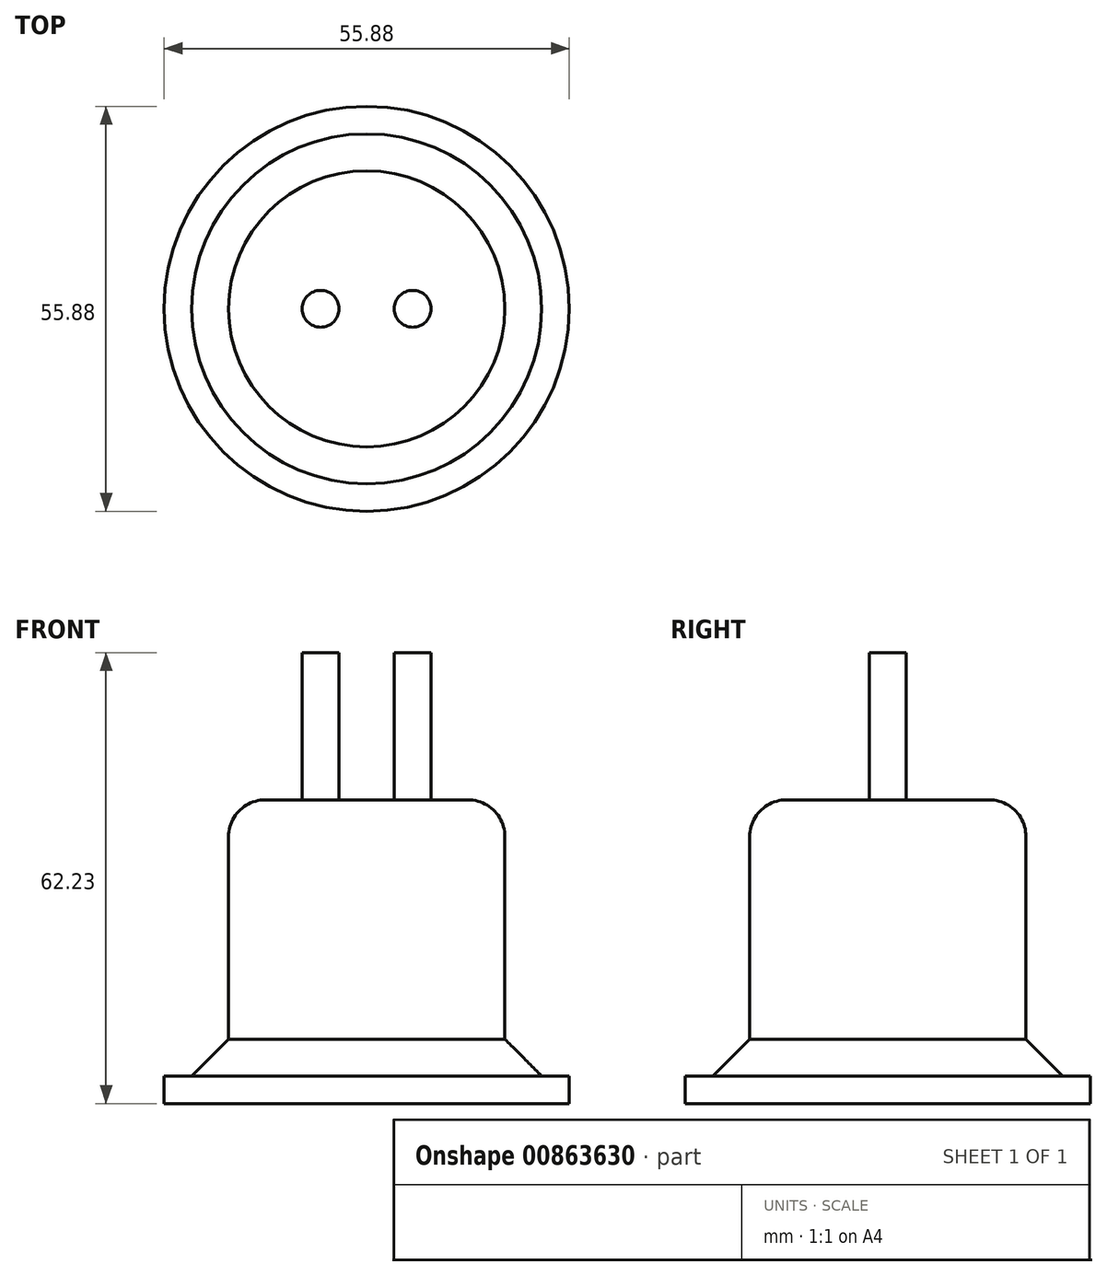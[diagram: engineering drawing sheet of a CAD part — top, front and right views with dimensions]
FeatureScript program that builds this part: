
annotation { "Feature Type Name" : "Feature", "Feature Type Description" : "" }
export const myFeature = defineFeature(function(context is Context, id is Id, definition is map)
    precondition{}
    {
        {
            var Q0;
            Q0=qCreatedBy(makeId("Top.planeOp"),FACE);
            var sketch = newSketch(context, id + "F0", { "sketchPlane" : qUnion([Q0])});
            skPoint(sketch, "E0.middle", {"position": v(0, 0) * mm});
            skCircle(sketch, "E1", {"center": v(0, 0) * mm, "radius": 27.94 * mm});
            skSolve(sketch);
        }
        {
            var Q0;
            Q0 = qSketchRegion(id + "F0", true);
            extrude(context, id + "F1", {"entities" : qUnion([Q0]), "depth" : 3.8 * mm, "offsetDistance" : 25.4 * mm});
        }
        {
            var Q0;
            Q0=makeQuery(id+"F1.opExtrude","CAP_FACE",FACE,{"disambiguationData":[OSD([sQuery(id+"F0.wireOp",EDGE,"E1")])],"isStart":false});
            var sketch = newSketch(context, id + "F2", { "sketchPlane" : qUnion([Q0])});
            skCircle(sketch, "E2", {"center": v(0, 0) * mm, "radius": 19.05 * mm});
            skSolve(sketch);
        }
        {
            var Q0;
            Q0=makeQuery(id+"F2.imprint","IMPRINT",FACE,{"disambiguationData":[TD([[makeQuery(id+"F2.imprint","IMPRINT",EDGE,{"derivedFrom":sQuery(id+"F2.wireOp",EDGE,"E2")}),1.0]])]});
            extrude(context, id + "F3", {"entities" : qUnion([Q0]), "operationType" : NewBodyOperationType.ADD, "depth" : 38.1 * mm, "offsetDistance" : 25.4 * mm});
        }
        {
            var Q0;
            Q0=makeQuery(id+"F3.opExtrude","CAP_FACE",FACE,{"disambiguationData":[OSD([sQuery(id+"F2.wireOp",EDGE,"E2")])],"isStart":false});
            fillet(context, id + "F4", {"entities" : qUnion([Q0]), "radius" : 5.08 * mm, "tangentPropagation" : true, "allowEdgeOverflow" : false});
        }
        {
            var Q0;
            Q0=makeQuery(id+"F3.opExtrude","SWEPT_FACE",FACE,{"disambiguationData":[OSD([sQuery(id+"F2.wireOp",EDGE,"E2")])]});
            chamfer(context, id + "F5", {"entities" : qUnion([Q0]), "width" : 5.08 * mm, "tangentPropagation" : true});
        }
        {
            var Q0;
            Q0=makeQuery(id+"F3.opExtrude","CAP_FACE",FACE,{"disambiguationData":[OSD([sQuery(id+"F2.wireOp",EDGE,"E2")])],"isStart":false});
            var sketch = newSketch(context, id + "F6", { "sketchPlane" : qUnion([Q0])});
            skCircle(sketch, "E3", {"center": v(-6.35, 0) * mm, "radius": 2.54 * mm});
            skCircle(sketch, "E4", {"center": v(6.35, 0) * mm, "radius": 2.54 * mm});
            skSolve(sketch);
        }
        {
            var Q0;
            Q0 = qSketchRegion(id + "F6", true);
            extrude(context, id + "F7", {"entities" : qUnion([Q0]), "operationType" : NewBodyOperationType.ADD, "depth" : 20.32 * mm, "offsetDistance" : 25.4 * mm});
        }
    });
